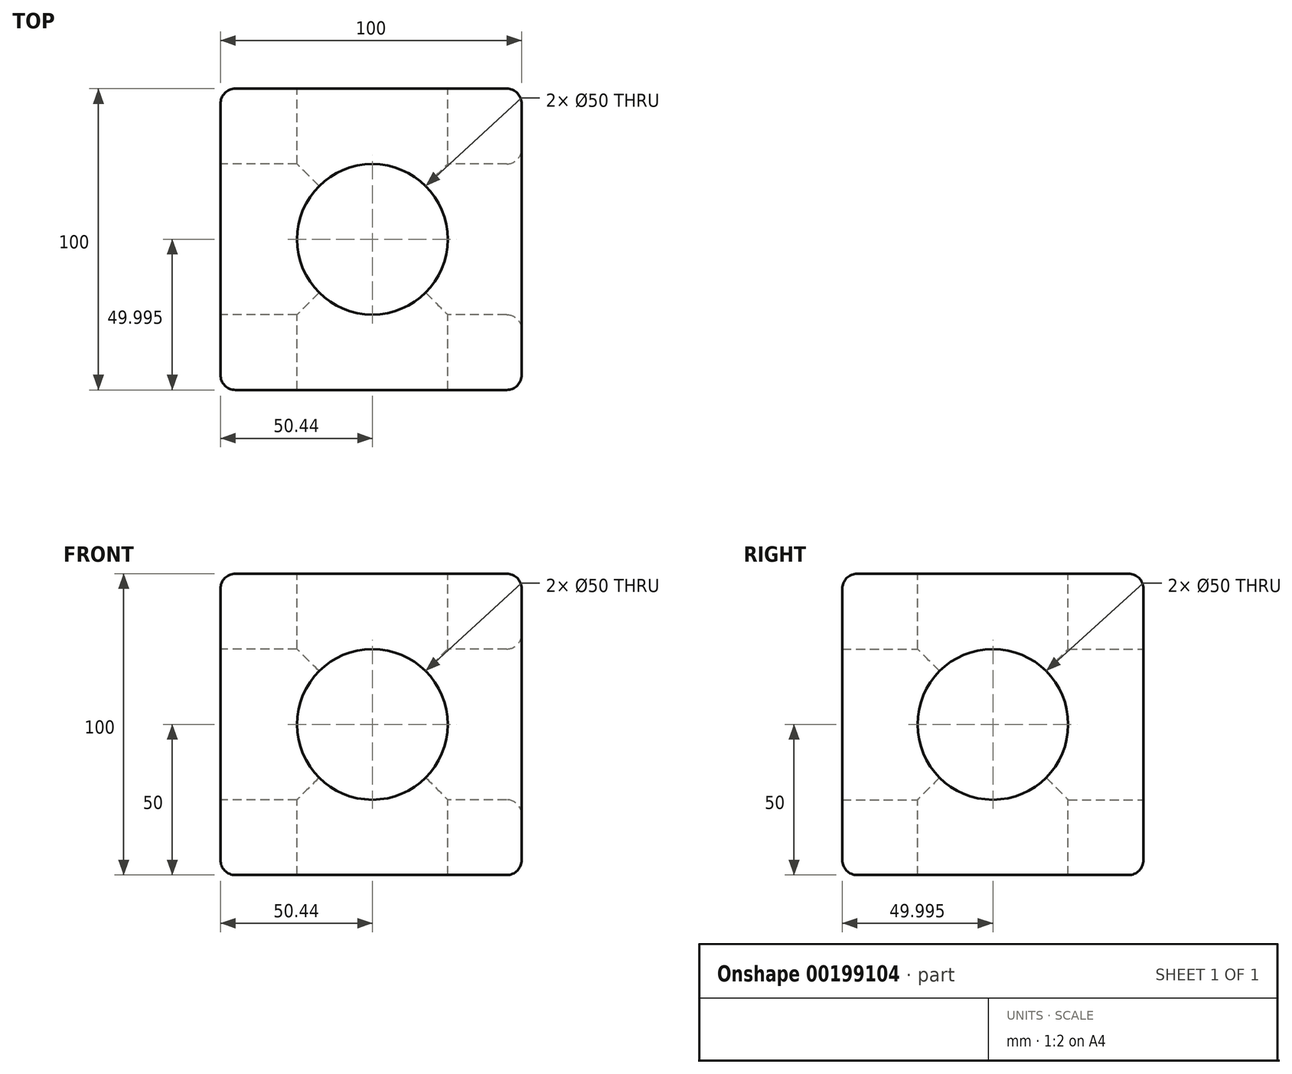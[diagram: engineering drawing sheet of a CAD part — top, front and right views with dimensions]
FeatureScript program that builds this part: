
annotation { "Feature Type Name" : "Feature", "Feature Type Description" : "" }
export const myFeature = defineFeature(function(context is Context, id is Id, definition is map)
    precondition{}
    {
        {
            var Q0;
            Q0=qCreatedBy(makeId("Top.planeOp"),FACE);
            var sketch = newSketch(context, id + "F0", { "sketchPlane" : qUnion([Q0])});
            skLineSegment(sketch, "E0.bottom", {"start": v(-50.44, 39.37) * mm, "end": v(49.56, 39.37) * mm});
            skLineSegment(sketch, "E0.top", {"start": v(-50.44, -60.63) * mm, "end": v(49.56, -60.63) * mm});
            skLineSegment(sketch, "E0.left", {"start": v(-50.44, 39.37) * mm, "end": v(-50.44, -60.63) * mm});
            skLineSegment(sketch, "E0.right", {"start": v(49.56, 39.37) * mm, "end": v(49.56, -60.63) * mm});
            skSolve(sketch);
        }
        {
            var Q0;
            Q0=makeQuery(id+"F0.imprint","IMPRINT",FACE,{"disambiguationData":[TD([[makeQuery(id+"F0.imprint","IMPRINT",EDGE,{"derivedFrom":sQuery(id+"F0.wireOp",EDGE,"E0.bottom")}),-1.0]])]});
            extrude(context, id + "F1", {"entities" : qUnion([Q0]), "depth" : 100 * mm});
        }
        {
            var Q0;
            Q0=makeQuery(id+"F1.opExtrude","CAP_EDGE",EDGE,{"disambiguationData":[OSD([sQuery(id+"F0.wireOp",EDGE,"E0.right")])],"isStart":false});
            var Q1;
            Q1=makeQuery(id+"F1.opExtrude","SWEPT_EDGE",EDGE,{"disambiguationData":[OSD([sQuery(id+"F0.wireOp",EDGE,"E0.top"),sQuery(id+"F0.wireOp",EDGE,"E0.right")])]});
            var Q2;
            Q2=makeQuery(id+"F1.opExtrude","CAP_EDGE",EDGE,{"disambiguationData":[OSD([sQuery(id+"F0.wireOp",EDGE,"E0.top")])],"isStart":false});
            var Q3;
            Q3=makeQuery(id+"F1.opExtrude","CAP_EDGE",EDGE,{"disambiguationData":[OSD([sQuery(id+"F0.wireOp",EDGE,"E0.left")])],"isStart":false});
            var Q4;
            Q4=makeQuery(id+"F1.opExtrude","CAP_EDGE",EDGE,{"disambiguationData":[OSD([sQuery(id+"F0.wireOp",EDGE,"E0.bottom")])],"isStart":false});
            var Q5;
            Q5=makeQuery(id+"F1.opExtrude","SWEPT_EDGE",EDGE,{"disambiguationData":[OSD([sQuery(id+"F0.wireOp",EDGE,"E0.bottom"),sQuery(id+"F0.wireOp",EDGE,"E0.right")])]});
            var Q6;
            Q6=makeQuery(id+"F1.opExtrude","SWEPT_EDGE",EDGE,{"disambiguationData":[OSD([sQuery(id+"F0.wireOp",EDGE,"E0.bottom"),sQuery(id+"F0.wireOp",EDGE,"E0.left")])]});
            var Q7;
            Q7=makeQuery(id+"F1.opExtrude","CAP_EDGE",EDGE,{"disambiguationData":[OSD([sQuery(id+"F0.wireOp",EDGE,"E0.right")])],"isStart":true});
            var Q8;
            Q8=makeQuery(id+"F1.opExtrude","CAP_EDGE",EDGE,{"disambiguationData":[OSD([sQuery(id+"F0.wireOp",EDGE,"E0.bottom")])],"isStart":true});
            var Q9;
            Q9=makeQuery(id+"F1.opExtrude","CAP_EDGE",EDGE,{"disambiguationData":[OSD([sQuery(id+"F0.wireOp",EDGE,"E0.top")])],"isStart":true});
            var Q10;
            Q10=makeQuery(id+"F1.opExtrude","CAP_EDGE",EDGE,{"disambiguationData":[OSD([sQuery(id+"F0.wireOp",EDGE,"E0.left")])],"isStart":true});
            var Q11;
            Q11=makeQuery(id+"F1.opExtrude","SWEPT_EDGE",EDGE,{"disambiguationData":[OSD([sQuery(id+"F0.wireOp",EDGE,"E0.top"),sQuery(id+"F0.wireOp",EDGE,"E0.left")])]});
            fillet(context, id + "F2", {"entities" : qUnion([Q0, Q1, Q2, Q3, Q4, Q5, Q6, Q7, Q8, Q9, Q10, Q11]), "radius" : 5 * mm, "tangentPropagation" : true, "allowEdgeOverflow" : false});
        }
        {
            var Q0;
            Q0=makeQuery(id+"F1.opExtrude","CAP_FACE",FACE,{"disambiguationData":[OSD([sQuery(id+"F0.wireOp",EDGE,"E0.bottom"),sQuery(id+"F0.wireOp",EDGE,"E0.top"),sQuery(id+"F0.wireOp",EDGE,"E0.left"),sQuery(id+"F0.wireOp",EDGE,"E0.right")])],"isStart":false});
            var sketch = newSketch(context, id + "F3", { "sketchPlane" : qUnion([Q0])});
            skPoint(sketch, "E1", {"position": v(0, -10.63) * mm});
            skPoint(sketch, "E1.positionSnap0", {"position": v(-45.44, -10.63) * mm});
            skSolve(sketch);
        }
        {
            var Q0;
            Q0=sQuery(id+"F3.wireOp",VERTEX,"E1");
            var Q1;
            Q1=makeQuery(id+"F1.opExtrude","SWEPT_BODY",BODY,{"disambiguationData":[OSD([sQuery(id+"F0.wireOp",EDGE,"E0.bottom"),sQuery(id+"F0.wireOp",EDGE,"E0.top"),sQuery(id+"F0.wireOp",EDGE,"E0.left"),sQuery(id+"F0.wireOp",EDGE,"E0.right")])]});
            hole(context, id + "F4", {"style" : HoleStyle.SIMPLE, "endStyle" : HoleEndStyle.THROUGH, "holeDiameter" : 50 * mm, "locations" : qUnion([Q0]), "scope" : qUnion([Q1]), "isTappedThrough" : true});
        }
        {
            var Q0;
            Q0=makeQuery(id+"F1.opExtrude","SWEPT_FACE",FACE,{"disambiguationData":[OSD([sQuery(id+"F0.wireOp",EDGE,"E0.bottom")])]});
            var sketch = newSketch(context, id + "F5", { "sketchPlane" : qUnion([Q0])});
            skPoint(sketch, "E2", {"position": v(0, 50) * mm});
            skPoint(sketch, "E2.positionSnap0", {"position": v(-44.56, 50) * mm});
            skSolve(sketch);
        }
        {
            var Q0;
            Q0=sQuery(id+"F5.wireOp",VERTEX,"E2");
            var Q1;
            Q1=makeQuery(id+"F1.opExtrude","SWEPT_BODY",BODY,{"disambiguationData":[OSD([sQuery(id+"F0.wireOp",EDGE,"E0.bottom"),sQuery(id+"F0.wireOp",EDGE,"E0.top"),sQuery(id+"F0.wireOp",EDGE,"E0.left"),sQuery(id+"F0.wireOp",EDGE,"E0.right")])]});
            hole(context, id + "F6", {"style" : HoleStyle.SIMPLE, "endStyle" : HoleEndStyle.THROUGH, "holeDiameter" : 50 * mm, "locations" : qUnion([Q0]), "scope" : qUnion([Q1]), "isTappedThrough" : true});
        }
        {
            var Q0;
            Q0=makeQuery(id+"F1.opExtrude","SWEPT_FACE",FACE,{"disambiguationData":[OSD([sQuery(id+"F0.wireOp",EDGE,"E0.left")])]});
            var sketch = newSketch(context, id + "F7", { "sketchPlane" : qUnion([Q0])});
            skPoint(sketch, "E3", {"position": v(10.63, 50) * mm});
            skPoint(sketch, "E3.positionSnap0", {"position": v(-34.37, 50) * mm});
            skPoint(sketch, "E3.positionSnap1", {"position": v(10.63, 5) * mm});
            skSolve(sketch);
        }
        {
            var Q0;
            Q0=sQuery(id+"F7.wireOp",VERTEX,"E3");
            var Q1;
            Q1=makeQuery(id+"F1.opExtrude","SWEPT_BODY",BODY,{"disambiguationData":[OSD([sQuery(id+"F0.wireOp",EDGE,"E0.bottom"),sQuery(id+"F0.wireOp",EDGE,"E0.top"),sQuery(id+"F0.wireOp",EDGE,"E0.left"),sQuery(id+"F0.wireOp",EDGE,"E0.right")])]});
            hole(context, id + "F8", {"style" : HoleStyle.SIMPLE, "endStyle" : HoleEndStyle.THROUGH, "holeDiameter" : 50 * mm, "locations" : qUnion([Q0]), "scope" : qUnion([Q1]), "isTappedThrough" : true});
        }
        {
            var Q0;
            Q0=makeQuery(id+"F6.hole-0.boolean.opBoolean","INTERSECT",EDGE,{"derivedFrom":[makeQuery(id+"F1.opExtrude","SWEPT_FACE",FACE,{"disambiguationData":[OSD([sQuery(id+"F0.wireOp",EDGE,"E0.top")])]}),makeQuery(id+"F6.hole-0.opRevolve","SWEPT_FACE",FACE,{"disambiguationData":[OSD([sQuery(id+"F6.hole-0.sketch.wireOp",EDGE,"core_line_2")])]})]});
            var Q1;
            Q1=makeQuery(id+"F6.hole-0.boolean.opBoolean","COPY",EDGE,{"derivedFrom":makeQuery(id+"F6.hole-0.opRevolve","SWEPT_EDGE",EDGE,{"disambiguationData":[OSD([sQuery(id+"F6.hole-0.sketch.wireOp",EDGE,"core_line_2"),sQuery(id+"F6.hole-0.sketch.wireOp",EDGE,"core_line_3")])]})});
            var Q2;
            Q2=makeQuery(id+"F8.hole-0.boolean.opBoolean","COPY",EDGE,{"derivedFrom":makeQuery(id+"F8.hole-0.opRevolve","SWEPT_EDGE",EDGE,{"disambiguationData":[OSD([sQuery(id+"F8.hole-0.sketch.wireOp",EDGE,"core_line_2"),sQuery(id+"F8.hole-0.sketch.wireOp",EDGE,"core_line_3")])]})});
            var Q3;
            Q3=makeQuery(id+"F1.opExtrude","SWEPT_FACE",FACE,{"disambiguationData":[OSD([sQuery(id+"F0.wireOp",EDGE,"E0.right")])]});
            var Q4;
            Q4=makeQuery(id+"F4.hole-0.boolean.opBoolean","COPY",EDGE,{"derivedFrom":makeQuery(id+"F4.hole-0.opRevolve","SWEPT_EDGE",EDGE,{"disambiguationData":[OSD([sQuery(id+"F4.hole-0.sketch.wireOp",EDGE,"core_line_2"),sQuery(id+"F4.hole-0.sketch.wireOp",EDGE,"core_line_3")])]})});
            var Q5;
            Q5=makeQuery(id+"F4.hole-0.boolean.opBoolean","INTERSECT",EDGE,{"derivedFrom":[makeQuery(id+"F1.opExtrude","CAP_FACE",FACE,{"disambiguationData":[OSD([sQuery(id+"F0.wireOp",EDGE,"E0.bottom"),sQuery(id+"F0.wireOp",EDGE,"E0.top"),sQuery(id+"F0.wireOp",EDGE,"E0.left"),sQuery(id+"F0.wireOp",EDGE,"E0.right")])],"isStart":true}),makeQuery(id+"F4.hole-0.opRevolve","SWEPT_FACE",FACE,{"disambiguationData":[OSD([sQuery(id+"F4.hole-0.sketch.wireOp",EDGE,"core_line_2")])]})]});
            fillet(context, id + "F9", {"entities" : qUnion([Q0, Q1, Q2, Q3, Q4, Q5]), "radius" : 5 * mm, "tangentPropagation" : true, "allowEdgeOverflow" : false});
        }
    });
